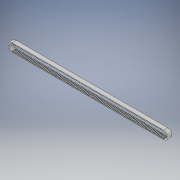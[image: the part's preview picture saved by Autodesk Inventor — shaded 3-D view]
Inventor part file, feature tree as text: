
AUTODESK INVENTOR PART (.ipt)
format: ipt  version: 2019 (Build 230136000, 136)  size: 1,205,248 bytes
history: native  units: mm
features: extrude x3, sketch x2, pattern_linear x2
ambient origin geometry x8: Origin, YZ Plane, XZ Plane, XY Plane, X Axis, Y Axis, Z Axis, Center Point
bodies: Solid1 (feature_tree)
feature tree (7):
  extrude  "Extrusion1"  Depth=12.0mm
  sketch  "Sketch2"  dims[d2=220.0mm d3=8.96mm d4=6.0mm d5=0.0mm d6=1.52mm d7=0.555mm d8=0.76mm d9=2.0mm d10=1.52mm d11=0.555mm d12=0.76mm d13=0.555mm d14=0.15mm d15=1.52mm d16=0.555mm d17=2.0mm d18=1.52mm d19=0.555mm d20=0.76mm d21=0.76mm d22=0.15mm d23=0.555mm d24=6.0mm d25=0.0mm d26=6.0mm d27=0.0mm d28=1100.0mm d30=1100.0mm]
  extrude  "Extrusion2"  Depth=6.0mm
  extrude  "Extrusion3"  Depth=6.0mm TaperAngle=0.0deg
  pattern_linear  "Rectangular Pattern1"  Spacing1=1.52mm  [1 undecoded]
  pattern_linear  "Rectangular Pattern2"  Spacing1=0.555mm  [1 undecoded]
  sketch  "Sketch1"  dims[d0=220.0mm d1=12.0mm]
note: 2 required parameter values undecoded (feature->parameter linkage not recoverable at this tier; creation-order binding heuristic only, values carry confidence <= 0.55)
